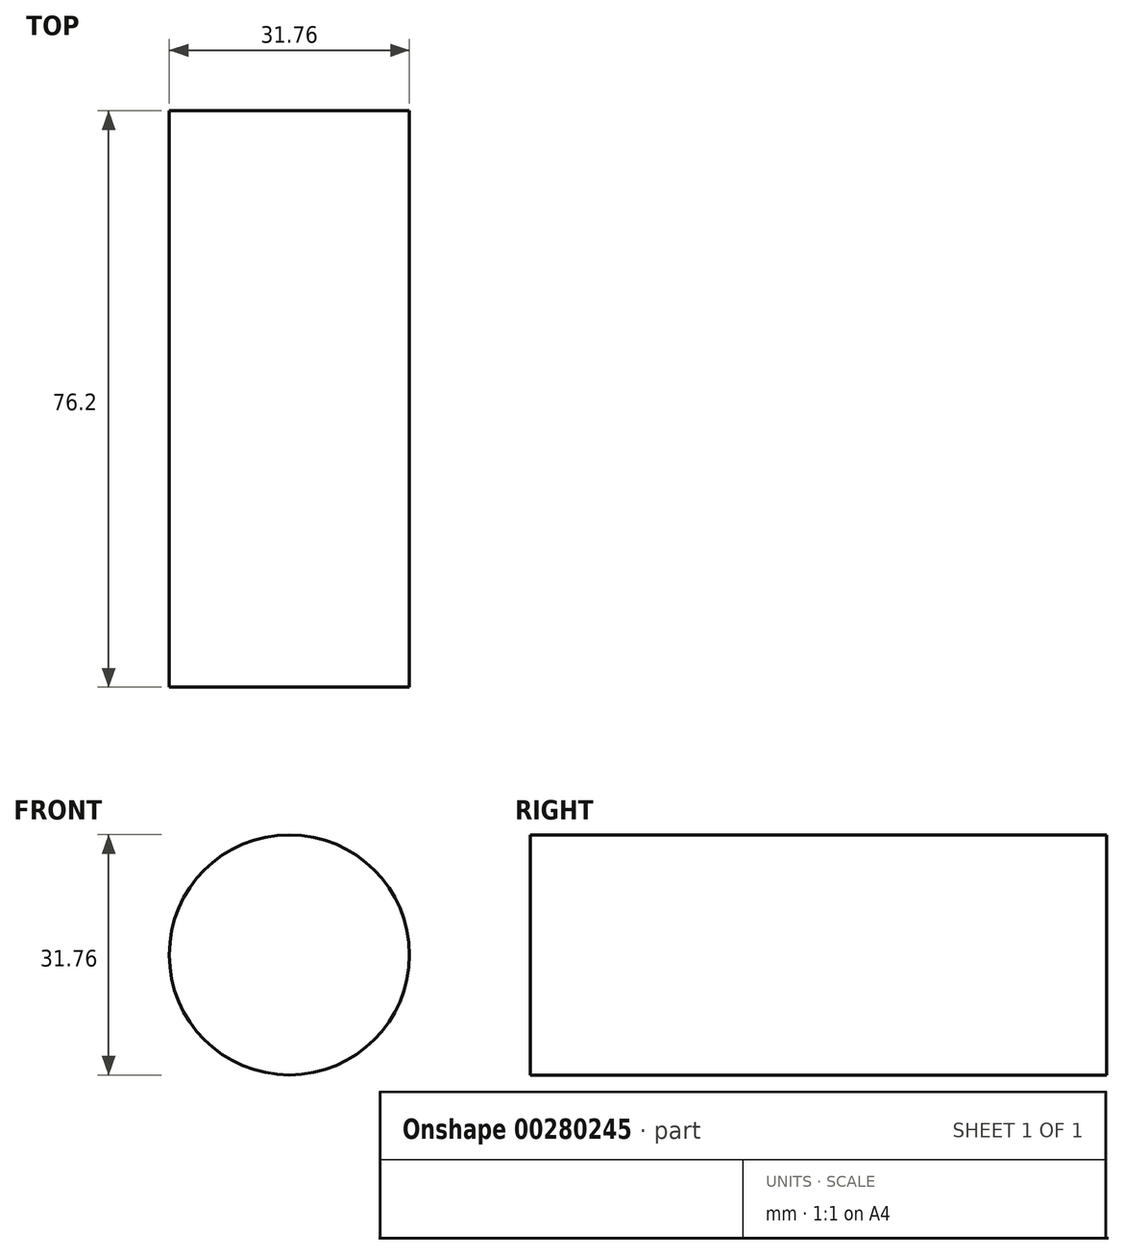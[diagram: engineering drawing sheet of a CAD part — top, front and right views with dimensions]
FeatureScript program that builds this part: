
annotation { "Feature Type Name" : "Feature", "Feature Type Description" : "" }
export const myFeature = defineFeature(function(context is Context, id is Id, definition is map)
    precondition{}
    {
        {
            var Q0;
            Q0=qCreatedBy(makeId("Front.planeOp"),FACE);
            var sketch = newSketch(context, id + "F0", { "sketchPlane" : qUnion([Q0])});
            skCircle(sketch, "E0", {"center": v(0, 0) * mm, "radius": 15.88 * mm});
            skSolve(sketch);
        }
        {
            var Q0;
            Q0 = qSketchRegion(id + "F0", true);
            extrude(context, id + "F1", {"entities" : qUnion([Q0]), "depth" : 76.2 * mm});
        }
    });
